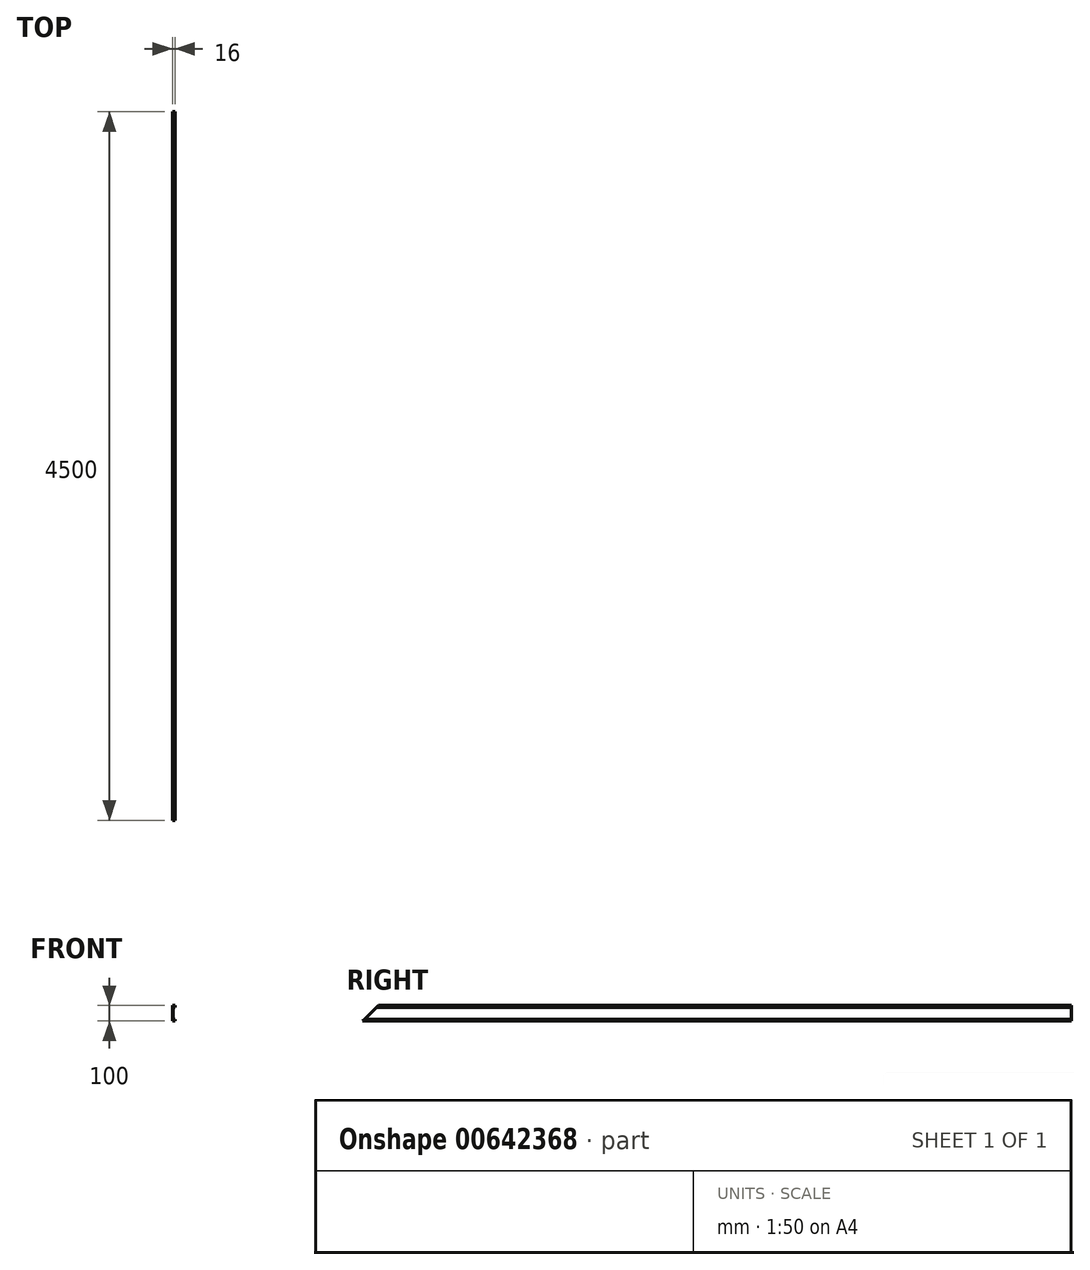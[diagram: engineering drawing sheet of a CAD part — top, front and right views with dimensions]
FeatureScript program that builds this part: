
annotation { "Feature Type Name" : "Feature", "Feature Type Description" : "" }
export const myFeature = defineFeature(function(context is Context, id is Id, definition is map)
    precondition{}
    {
        {
            var Q0;
            Q0=qCreatedBy(makeId("Front.planeOp"),FACE);
            var sketch = newSketch(context, id + "F0", { "sketchPlane" : qUnion([Q0])});
            skLineSegment(sketch, "E0", {"start": v(0, 0) * mm, "end": v(0, 100) * mm});
            skLineSegment(sketch, "E1", {"start": v(0, 100) * mm, "end": v(16, 100) * mm});
            skLineSegment(sketch, "E2", {"start": v(16, 100) * mm, "end": v(16, 88) * mm});
            skLineSegment(sketch, "E3", {"start": v(0, 0) * mm, "end": v(16, 0) * mm});
            skLineSegment(sketch, "E4", {"start": v(16, 0) * mm, "end": v(16, 12) * mm});
            skLineSegment(sketch, "E5.0", {"start": v(11, 95) * mm, "end": v(11, 88) * mm});
            skLineSegment(sketch, "E5.1", {"start": v(11, 5) * mm, "end": v(11, 12) * mm});
            skLineSegment(sketch, "E5.2", {"start": v(5, 5) * mm, "end": v(11, 5) * mm});
            skLineSegment(sketch, "E5.3", {"start": v(5, 5) * mm, "end": v(5, 95) * mm});
            skLineSegment(sketch, "E5.4", {"start": v(5, 95) * mm, "end": v(11, 95) * mm});
            skLineSegment(sketch, "E6", {"start": v(11, 12) * mm, "end": v(16, 12) * mm});
            skLineSegment(sketch, "E7", {"start": v(11, 88) * mm, "end": v(16, 88) * mm});
            skSolve(sketch);
        }
        {
            var Q0;
            Q0=makeQuery(id+"F0.imprint","IMPRINT",FACE,{"disambiguationData":[TD([[makeQuery(id+"F0.imprint","IMPRINT",EDGE,{"derivedFrom":sQuery(id+"F0.wireOp",EDGE,"E0")}),-1.0]])]});
            extrude(context, id + "F1", {"entities" : qUnion([Q0]), "endBound" : BoundingType.SYMMETRIC, "depth" : 4500 * mm, "offsetDistance" : 25 * mm});
        }
        {
            var Q0;
            Q0=makeQuery(id+"F1.opExtrude","SWEPT_FACE",FACE,{"disambiguationData":[OSD([sQuery(id+"F0.wireOp",EDGE,"E0")])]});
            var sketch = newSketch(context, id + "F2", { "sketchPlane" : qUnion([Q0])});
            skLineSegment(sketch, "E8", {"start": v(2250, 0) * mm, "end": v(2150, 100) * mm});
            skSolve(sketch);
        }
        {
            var Q0;
            {var subQ0=sQuery(id+"F2.wireOp",EDGE,"E8");Q0=makeQuery(id+"F2.imprint","IMPRINT",FACE,{"disambiguationData":[TD([[makeQuery(id+"F2.imprint","IMPRINT",EDGE,{"derivedFrom":subQ0}),-1.0]])]});}
            extrude(context, id + "F3", {"entities" : qUnion([Q0]), "operationType" : NewBodyOperationType.REMOVE, "oppositeDirection" : true, "depth" : 25 * mm, "offsetDistance" : 25 * mm});
        }
    });
